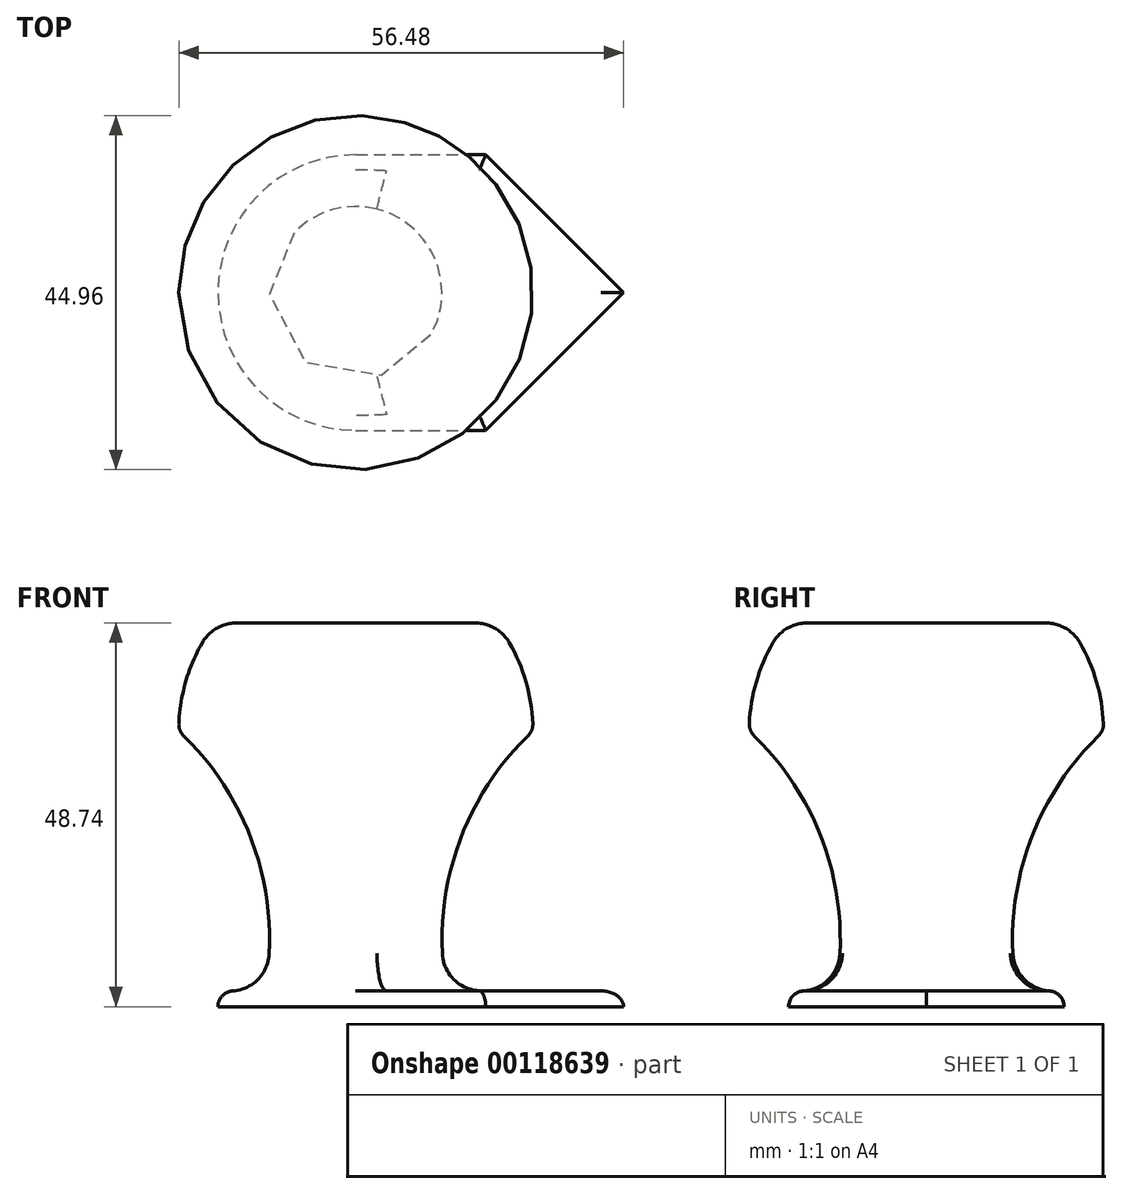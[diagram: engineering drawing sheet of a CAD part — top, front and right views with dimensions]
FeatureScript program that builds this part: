
annotation { "Feature Type Name" : "Feature", "Feature Type Description" : "" }
export const myFeature = defineFeature(function(context is Context, id is Id, definition is map)
    precondition{}
    {
        {
            var Q0;
            Q0=qCreatedBy(makeId("Front.planeOp"),FACE);
            var sketch = newSketch(context, id + "F0", { "sketchPlane" : qUnion([Q0])});
            skArc(sketch, "E0", {"start": v(22.5, 35) * mm, "mid": v(15.9, 50.9) * mm, "end": v(0, 57.5) * mm});
            skLineSegment(sketch, "E1", {"start": v(0, 91.14) * mm, "end": v(0, -25.27) * mm, "construction": true});
            skLineSegment(sketch, "E2", {"start": v(52.46, 35) * mm, "end": v(-58.12, 35) * mm, "construction": true});
            skArc(sketch, "E3", {"start": v(22.5, 35) * mm, "mid": v(12.48, 18.93) * mm, "end": v(11.97, 0) * mm});
            skLineSegment(sketch, "E4", {"start": v(11.97, 0) * mm, "end": v(0, 0) * mm});
            skLineSegment(sketch, "E5", {"start": v(0, 57.5) * mm, "end": v(0, 0) * mm});
            skSolve(sketch);
        }
        {
            var Q0;
            Q0 = qSketchRegion(id + "F0", true);
            var Q1;
            Q1=sQuery(id+"F0.wireOp",EDGE,"E5");
            revolve(context, id + "F1", {"entities" : qUnion([Q0]), "axis" : qUnion([Q1]), "revolveType" : RevolveType.FULL});
        }
        {
            var Q0;
            Q0=makeQuery(id+"F1.opRevolve","SWEPT_FACE",FACE,{"disambiguationData":[OSD([sQuery(id+"F0.wireOp",EDGE,"E4")])]});
            var sketch = newSketch(context, id + "F2", { "sketchPlane" : qUnion([Q0])});
            skArc(sketch, "E6", {"start": v(0, 17.5) * mm, "mid": v(-17.5, 0) * mm, "end": v(0, -17.5) * mm});
            skLineSegment(sketch, "E7", {"start": v(0, 17.5) * mm, "end": v(16.5, 17.5) * mm});
            skLineSegment(sketch, "E8", {"start": v(0, -17.5) * mm, "end": v(16.5, -17.5) * mm});
            skLineSegment(sketch, "E9", {"start": v(34, 0) * mm, "end": v(34, 25.32) * mm, "construction": true});
            skLineSegment(sketch, "E10", {"start": v(34, 0) * mm, "end": v(16.5, 17.5) * mm});
            skLineSegment(sketch, "E11.MirrorCS", {"start": v(34, 0) * mm, "end": v(16.5, -17.5) * mm});
            skPoint(sketch, "E12.orphan", {"position": v(11.09, 22.91) * mm});
            skPoint(sketch, "E13.orphan", {"position": v(11.09, -22.91) * mm});
            skPoint(sketch, "E14.orphan", {"position": v(47.73, -17.5) * mm});
            skLineSegment(sketch, "E15.trimOffspring", {"start": v(34, 17.5) * mm, "end": v(47.73, 17.5) * mm});
            skSolve(sketch);
        }
        {
            var Q0;
            Q0=makeQuery(id+"F2.imprint","IMPRINT",FACE,{"disambiguationData":[TD([[makeQuery(id+"F2.imprint","IMPRINT",EDGE,{"derivedFrom":sQuery(id+"F2.wireOp",EDGE,"E6")}),1.0]])]});
            var Q1;
            Q1=makeQuery(id+"F2.imprint","IMPRINT",FACE,{"disambiguationData":[TD([[makeQuery(id+"F2.imprint","IMPRINT",EDGE,{"derivedFrom":makeQuery(id+"F1.opRevolve","SWEPT_EDGE",EDGE,{"disambiguationData":[OSD([sQuery(id+"F0.wireOp",EDGE,"E3"),sQuery(id+"F0.wireOp",EDGE,"E4")])]})}),-1.0]])]});
            extrude(context, id + "F3", {"entities" : qUnion([Q0, Q1]), "operationType" : NewBodyOperationType.ADD, "oppositeDirection" : true, "depth" : 2 * mm});
        }
        {
            var Q0;
            Q0=makeQuery(id+"F3.opExtrude","CAP_EDGE",EDGE,{"disambiguationData":[OSD([sQuery(id+"F2.wireOp",EDGE,"E6")])],"isStart":false});
            var Q1;
            Q1=makeQuery(id+"F3.opExtrude","CAP_EDGE",EDGE,{"disambiguationData":[OSD([sQuery(id+"F2.wireOp",EDGE,"E10")])],"isStart":false});
            var Q2;
            Q2=makeQuery(id+"F3.opExtrude","CAP_EDGE",EDGE,{"disambiguationData":[OSD([sQuery(id+"F2.wireOp",EDGE,"E11.MirrorCS")])],"isStart":false});
            var Q3;
            Q3=makeQuery(id+"F1.opRevolve","SWEPT_EDGE",EDGE,{"disambiguationData":[OSD([sQuery(id+"F0.wireOp",EDGE,"E0"),sQuery(id+"F0.wireOp",EDGE,"E3")])]});
            fillet(context, id + "F4", {"entities" : qUnion([Q0, Q1, Q2, Q3]), "radius" : 2 * mm, "tangentPropagation" : true, "allowEdgeOverflow" : false});
        }
        {
            var Q0;
            Q0=makeQuery(id+"F3.boolean.opBoolean","INTERSECT",EDGE,{"derivedFrom":[makeQuery(id+"F1.opRevolve","SWEPT_FACE",FACE,{"disambiguationData":[OSD([sQuery(id+"F0.wireOp",EDGE,"E3")])]}),makeQuery(id+"F3.opExtrude","CAP_FACE",FACE,{"disambiguationData":[OSD([sQuery(id+"F2.wireOp",EDGE,"E6"),sQuery(id+"F2.wireOp",EDGE,"E7"),sQuery(id+"F2.wireOp",EDGE,"E8"),sQuery(id+"F2.wireOp",EDGE,"E10"),sQuery(id+"F2.wireOp",EDGE,"E11.MirrorCS")])],"isStart":false})]});
            fillet(context, id + "F5", {"entities" : qUnion([Q0]), "radius" : 5 * mm, "tangentPropagation" : true, "allowEdgeOverflow" : false});
        }
        {
            var Q0;
            Q0=qCreatedBy(makeId("Right.planeOp"),FACE);
            var sketch = newSketch(context, id + "F6", { "sketchPlane" : qUnion([Q0])});
            skLineSegment(sketch, "E16", {"start": v(-39.26, 48.74) * mm, "end": v(41, 48.74) * mm});
            skLineSegment(sketch, "E17", {"start": v(41, 48.74) * mm, "end": v(0, 68.5) * mm});
            skLineSegment(sketch, "E18", {"start": v(0, 68.5) * mm, "end": v(-39.26, 48.74) * mm});
            skSolve(sketch);
        }
        {
            var Q0;
            Q0 = qSketchRegion(id + "F6", true);
            extrude(context, id + "F7", {"entities" : qUnion([Q0]), "operationType" : NewBodyOperationType.REMOVE, "oppositeDirection" : true, "depth" : 25 * mm, "hasSecondDirection" : true, "secondDirectionOppositeDirection" : false, "secondDirectionDepth" : 25 * mm});
        }
        {
            var Q0;
            Q0=makeQuery(id+"F7.boolean.opBoolean","INTERSECT",EDGE,{"derivedFrom":[makeQuery(id+"F1.opRevolve","SWEPT_FACE",FACE,{"disambiguationData":[OSD([sQuery(id+"F0.wireOp",EDGE,"E0")])]}),makeQuery(id+"F7.opExtrude","SWEPT_FACE",FACE,{"disambiguationData":[OSD([sQuery(id+"F6.wireOp",EDGE,"E16")])]})]});
            fillet(context, id + "F8", {"entities" : qUnion([Q0]), "radius" : 5 * mm, "tangentPropagation" : true, "allowEdgeOverflow" : false});
        }
    });
